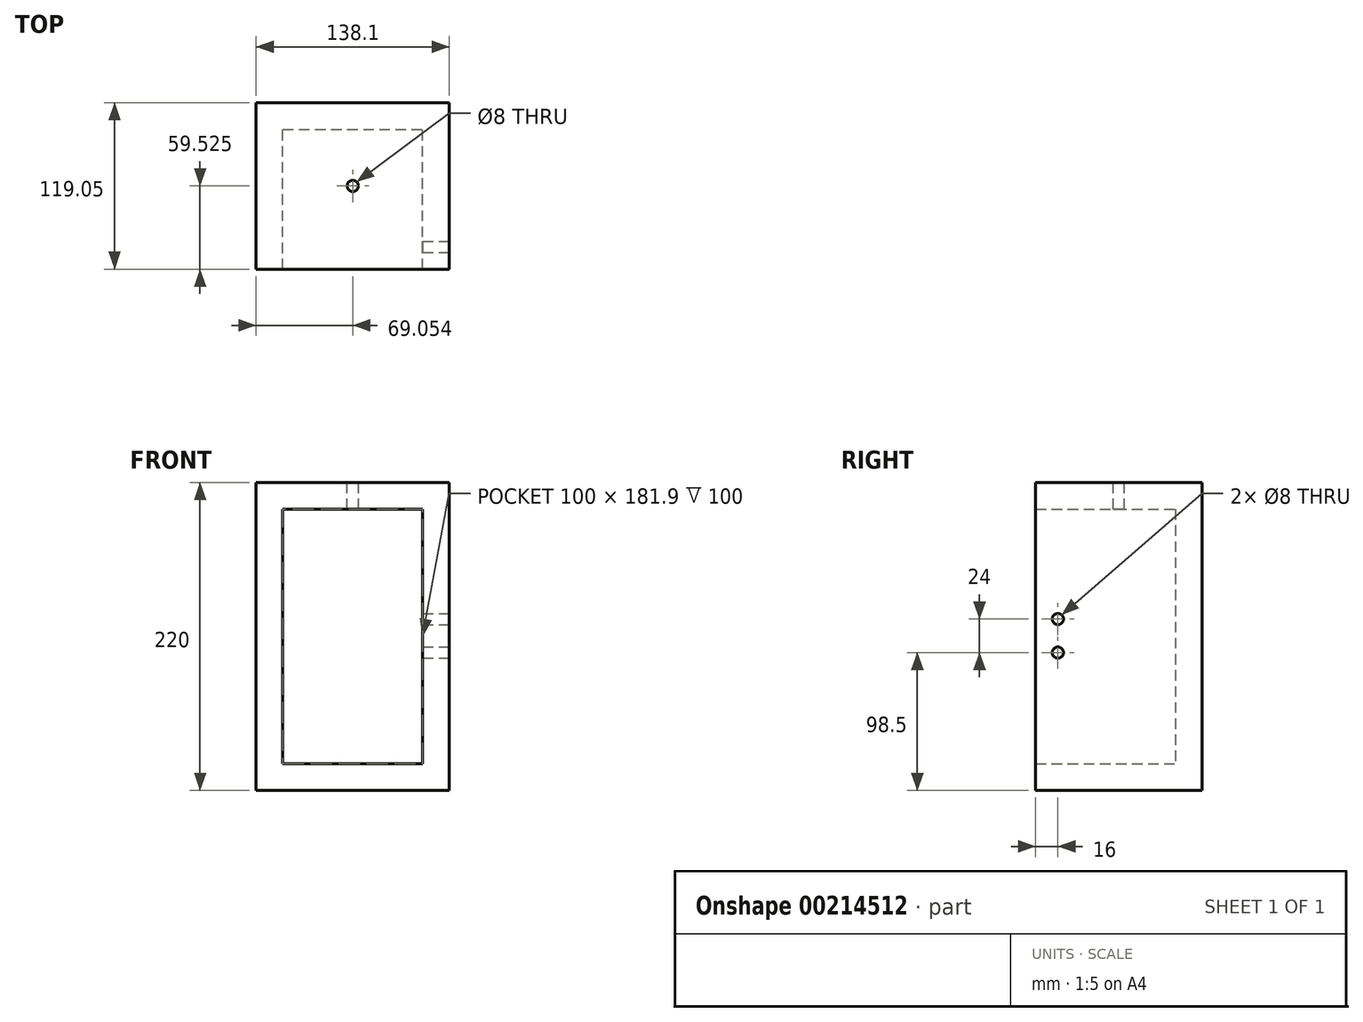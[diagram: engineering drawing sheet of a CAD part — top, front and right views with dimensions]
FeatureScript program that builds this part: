
annotation { "Feature Type Name" : "Feature", "Feature Type Description" : "" }
export const myFeature = defineFeature(function(context is Context, id is Id, definition is map)
    precondition{}
    {
        {
            var Q0;
            Q0=qCreatedBy(makeId("Top.planeOp"),FACE);
            cPlane(context, id + "F0", {"entities" : qUnion([Q0]), "cplaneType" : CPlaneType.OFFSET, "offset" : 5.5 * mm, "oppositeDirection" : true, "width" : 150 * mm, "height" : 150 * mm});
        }
        {
            var Q0;
            Q0=qCreatedBy(id+"F0.planeOp",FACE);
            var sketch = newSketch(context, id + "F1", { "sketchPlane" : qUnion([Q0])});
            skLineSegment(sketch, "E0.bottom", {"start": v(-55.15, 50) * mm, "end": v(44.85, 50) * mm});
            skLineSegment(sketch, "E0.top", {"start": v(-55.15, -50) * mm, "end": v(44.85, -50) * mm, "construction": true});
            skLineSegment(sketch, "E0.left", {"start": v(-55.15, 50) * mm, "end": v(-55.15, -50) * mm});
            skLineSegment(sketch, "E0.right", {"start": v(44.85, 50) * mm, "end": v(44.85, -50) * mm});
            skPoint(sketch, "E0.middle", {"position": v(-5.15, 0) * mm});
            skLineSegment(sketch, "E1.0", {"start": v(-74.2, 69.05) * mm, "end": v(63.9, 69.05) * mm});
            skLineSegment(sketch, "E2.0", {"start": v(63.9, 69.05) * mm, "end": v(63.9, -50) * mm});
            skLineSegment(sketch, "E3.0", {"start": v(-74.2, 69.05) * mm, "end": v(-74.2, -50) * mm});
            skLineSegment(sketch, "E4", {"start": v(-74.2, -50) * mm, "end": v(-55.15, -50) * mm});
            skLineSegment(sketch, "E5", {"start": v(44.85, -50) * mm, "end": v(63.9, -50) * mm});
            skSolve(sketch);
        }
        {
            var Q0;
            Q0 = qSketchRegion(id + "F1", true);
            extrude(context, id + "F2", {"entities" : qUnion([Q0]), "depth" : 140 * mm, "hasSecondDirection" : true, "secondDirectionOppositeDirection" : true, "secondDirectionDepth" : 80 * mm});
        }
        {
            var Q0;
            Q0=makeQuery(id+"F2.opExtrude","SWEPT_FACE",FACE,{"disambiguationData":[OSD([sQuery(id+"F1.wireOp",EDGE,"E0.bottom")])]});
            var sketch = newSketch(context, id + "F3", { "sketchPlane" : qUnion([Q0])});
            skLineSegment(sketch, "E6.bottom", {"start": v(-55.15, 134.5) * mm, "end": v(44.85, 134.5) * mm});
            skLineSegment(sketch, "E6.top", {"start": v(-55.15, 115.45) * mm, "end": v(44.85, 115.45) * mm});
            skLineSegment(sketch, "E6.left", {"start": v(-55.15, 134.5) * mm, "end": v(-55.15, 115.45) * mm});
            skLineSegment(sketch, "E6.right", {"start": v(44.85, 134.5) * mm, "end": v(44.85, 115.45) * mm});
            skLineSegment(sketch, "E7.bottom", {"start": v(-55.15, -85.5) * mm, "end": v(44.85, -85.5) * mm});
            skLineSegment(sketch, "E7.top", {"start": v(-55.15, -66.45) * mm, "end": v(44.85, -66.45) * mm});
            skLineSegment(sketch, "E7.left", {"start": v(-55.15, -85.5) * mm, "end": v(-55.15, -66.45) * mm});
            skLineSegment(sketch, "E7.right", {"start": v(44.85, -85.5) * mm, "end": v(44.85, -66.45) * mm});
            skSolve(sketch);
        }
        {
            var Q0;
            Q0 = qSketchRegion(id + "F3", true);
            extrude(context, id + "F4", {"entities" : qUnion([Q0]), "operationType" : NewBodyOperationType.ADD, "depth" : 100 * mm});
        }
        {
            var Q0;
            Q0=makeQuery(id+"F4.boolean.opBoolean","MERGE",FACE,{"derivedFrom":[makeQuery(id+"F2.opExtrude","CAP_FACE",FACE,{"disambiguationData":[OSD([sQuery(id+"F1.wireOp",EDGE,"E0.bottom"),sQuery(id+"F1.wireOp",EDGE,"E0.left"),sQuery(id+"F1.wireOp",EDGE,"E0.right"),sQuery(id+"F1.wireOp",EDGE,"E1.0"),sQuery(id+"F1.wireOp",EDGE,"E2.0"),sQuery(id+"F1.wireOp",EDGE,"E3.0"),sQuery(id+"F1.wireOp",EDGE,"E4"),sQuery(id+"F1.wireOp",EDGE,"E5")])],"isStart":false}),makeQuery(id+"F4.opExtrude","SWEPT_FACE",FACE,{"disambiguationData":[OSD([sQuery(id+"F3.wireOp",EDGE,"E6.bottom")])]})]});
            var sketch = newSketch(context, id + "F5", { "sketchPlane" : qUnion([Q0])});
            skCircle(sketch, "E8", {"center": v(-5.15, 9.52) * mm, "radius": 4 * mm});
            skLineSegment(sketch, "E9", {"start": v(-74.2, 69.05) * mm, "end": v(63.9, 69.05) * mm, "construction": true});
            skLineSegment(sketch, "E10", {"start": v(63.9, 69.05) * mm, "end": v(63.9, 50) * mm, "construction": true});
            skLineSegment(sketch, "E11", {"start": v(63.9, 50) * mm, "end": v(-74.2, 50) * mm, "construction": true});
            skLineSegment(sketch, "E12", {"start": v(-74.2, 50) * mm, "end": v(-74.2, -50) * mm, "construction": true});
            skPoint(sketch, "E13", {"position": v(-5.15, 50) * mm});
            skPoint(sketch, "E14", {"position": v(-74.2, 9.52) * mm});
            skSolve(sketch);
        }
        {
            var Q0;
            Q0 = qSketchRegion(id + "F5", true);
            extrude(context, id + "F6", {"entities" : qUnion([Q0]), "operationType" : NewBodyOperationType.REMOVE, "oppositeDirection" : true, "depth" : 19.05 * mm});
        }
        {
            var Q0;
            Q0=makeQuery(id+"F2.opExtrude","SWEPT_FACE",FACE,{"disambiguationData":[OSD([sQuery(id+"F1.wireOp",EDGE,"E2.0")])]});
            var sketch = newSketch(context, id + "F7", { "sketchPlane" : qUnion([Q0])});
            skLineSegment(sketch, "E15", {"start": v(-41.4, 13) * mm, "end": v(26.55, 13) * mm, "construction": true});
            skLineSegment(sketch, "E16.0", {"start": v(-41.4, 37) * mm, "end": v(26.55, 37) * mm, "construction": true});
            skLineSegment(sketch, "E17", {"start": v(-50, 0) * mm, "end": v(-50, 55.6) * mm, "construction": true});
            skLineSegment(sketch, "E18.0", {"start": v(-34, 0) * mm, "end": v(-34, 55.6) * mm, "construction": true});
            skCircle(sketch, "E19", {"center": v(-34, 13) * mm, "radius": 4 * mm});
            skCircle(sketch, "E20", {"center": v(-34, 37) * mm, "radius": 4 * mm});
            skSolve(sketch);
        }
        {
            var Q0;
            Q0 = qSketchRegion(id + "F7", true);
            extrude(context, id + "F8", {"entities" : qUnion([Q0]), "operationType" : NewBodyOperationType.REMOVE, "oppositeDirection" : true, "depth" : 20 * mm});
        }
    });
